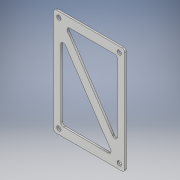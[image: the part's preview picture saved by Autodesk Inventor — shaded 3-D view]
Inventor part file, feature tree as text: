
AUTODESK INVENTOR PART (.ipt)
format: ipt  version: 2019 (Build 230136000, 136)  size: 141,824 bytes
history: native  units: mm
features: extrude x1, sketch x1
ambient origin geometry x8: Origin, YZ Plane, XZ Plane, XY Plane, X Axis, Y Axis, Z Axis, Center Point
bodies: Body1 (feature_tree)
feature tree (2):
  extrude  "Extrusion3"  Depth=50.0mm
  sketch  "Sketch1"  dims[d5=15.0mm d7=50.0mm d8=50.0mm d14=40.0mm d15=40.0mm d16=40.0mm d17=40.0mm d20=25.0mm d21=30.0mm d22=30.0mm d23=10.0mm d24=0.0mm]
